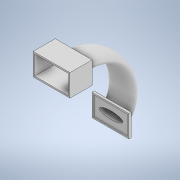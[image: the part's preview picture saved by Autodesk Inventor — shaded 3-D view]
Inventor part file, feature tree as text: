
AUTODESK INVENTOR PART (.ipt)
format: ipt  version: 2021 (Build 250183000, 183)  size: 857,088 bytes
history: native  units: mm
features: sketch x6, extrude x3, plane x1, sweep x1, shell x1
ambient origin geometry x8: Origin, YZ Plane, XZ Plane, XY Plane, X Axis, Y Axis, Z Axis, Center Point
bodies: Volumenkörper1 (feature_tree)
feature tree (12):
  extrude  "Extrusion1"  Depth=30.0mm
  sketch  "Skizze2"  dims[d2=30.0mm d3=0.0mm d4=15.0mm]
  sketch  "Skizze3"  dims[d5=25.0mm d6=18.0mm d7=7.0mm]
  plane  "Arbeitsebene1"
  extrude  "Extrusion2"  Depth=15.0mm
  sweep  "Sweeping1"
  shell  "Wandung1"  Thickness=7.0mm
  extrude  "Extrusion3"  Depth=50.0mm
  sketch  "Skizze1"  dims[d0=50.0mm d1=30.0mm]
  sketch  "Skizze4"  dims[d8=53.0mm d9=50.0mm]
  sketch  "Skizze5"  dims[d10=30.0mm]
  sketch  "Skizze6"  dims[d11=58.0mm d12=3.0mm d13=0.0mm d32=77.124757mm d33=117.013795mm d34=88.0mm d35=0.0mm d36=0.0mm d37=2.0mm d38=2.0mm d39=25.0mm d40=0.0mm]
